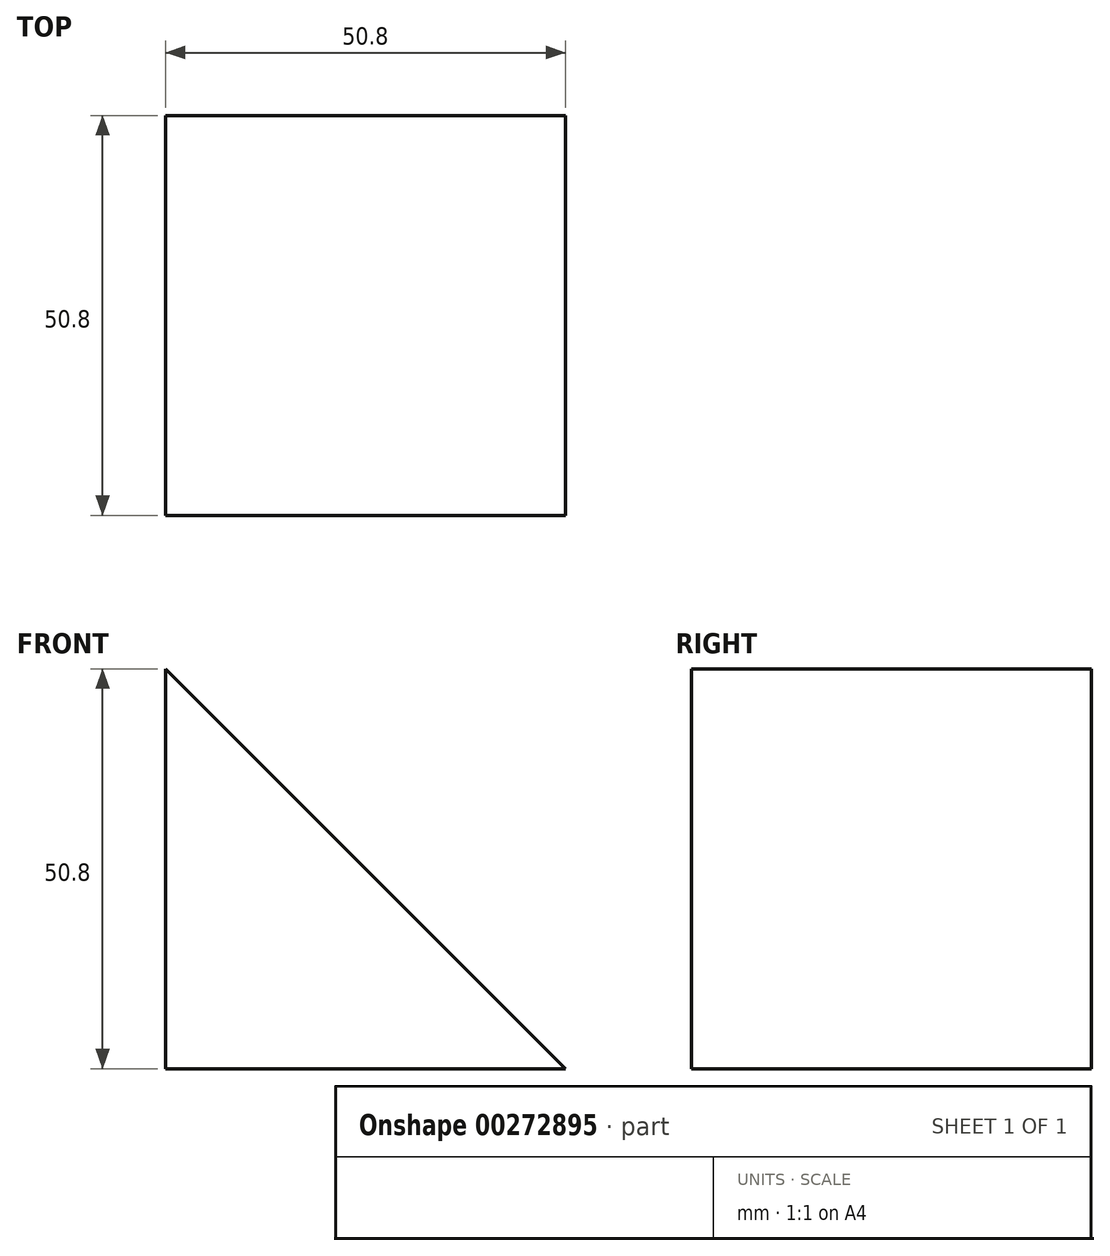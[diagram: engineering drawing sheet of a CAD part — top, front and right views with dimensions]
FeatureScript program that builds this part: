
annotation { "Feature Type Name" : "Feature", "Feature Type Description" : "" }
export const myFeature = defineFeature(function(context is Context, id is Id, definition is map)
    precondition{}
    {
        {
            var Q0;
            Q0=qCreatedBy(makeId("Front.planeOp"),FACE);
            var sketch = newSketch(context, id + "F0", { "sketchPlane" : qUnion([Q0])});
            skLineSegment(sketch, "E0", {"start": v(-47.93, 65.12) * mm, "end": v(-47.93, 14.32) * mm});
            skLineSegment(sketch, "E1", {"start": v(-47.93, 14.32) * mm, "end": v(2.87, 14.32) * mm});
            skLineSegment(sketch, "E2", {"start": v(2.87, 14.32) * mm, "end": v(-47.93, 65.12) * mm});
            skSolve(sketch);
        }
        {
            var Q0;
            Q0=makeQuery(id+"F0.imprint","IMPRINT",FACE,{"disambiguationData":[TD([[makeQuery(id+"F0.imprint","IMPRINT",EDGE,{"derivedFrom":sQuery(id+"F0.wireOp",EDGE,"E0")}),1.0]])]});
            extrude(context, id + "F1", {"entities" : qUnion([Q0]), "depth" : 50.8 * mm});
        }
    });
